# Revit family: QF_Varimixer_Teddy5L
name_source: partatom
category: Specialty Equipment
units: mm (PartAtom-declared; Revit-internal decimal feet)

## family parameters
Always vertical = Yes
Cut with Voids When Loaded = No
OmniClass Number = 23.40.40.14.14.11
OmniClass Title = Food Mixers
Part Type = Normal
Room Calculation Point = No
Round Connector Dimension = Use Diameter
Shared = No
Work Plane-Based = No

## types (15) — shared parameters
Bowl size = 5 liter
Connected with neutral = No
Depth = 462 mm  [stored 1.51575 ft]
Depth Clearance = 540 mm
Description = Planetary mixer TEDDY
Electrical connection height = 40 mm  [stored 0.131234 ft]
Height = 400 mm
Homepage = https://www.varimixer.com
Horsepower = 0.4
Ingress protection = IP42
Length = 241 mm
Manufacturer = Varimixer A/S
Model = TEDDY
Number of phases = 1
Plug included = Yes
Power = 300 W
Product description = Planetary mixer, heavy duty for whipping, kneading and mixing
Product name = TEDDY
URL = www.varimixer.com
URL datasheet = https://varimixer.com
Weight in Kilograms = 18
Weight in Pounds = 40

## per-type parameters (varying)
| type | Attachment drive | Color | Cycle | Full load current | Voltage |
| 230V/50-60Hz/1Ph/Red | No | QF_Plastic-Red-Smooth | 50 Hz | 2 A | 230 V |
| 230V/50-60Hz/1Ph/White | No | QF_Plastic-White-Smooth | 50 Hz | 2 A | 230 V |
| 230V/50-60Hz/1Ph/Silver | No | QF_Metal-Stainless-Satin Brushed Heavy | 50 Hz | 2 A | 230 V |
| 230V/50-60Hz/1Ph/Black | No | QF_Plastic-Black-Smooth | 50 Hz | 2 A | 230 V |
| 230V/50-60Hz/1Ph/White atttachmentdrive | Yes | QF_Plastic-White-Smooth | 50 Hz | 2 A | 230 V |
| 115V/50-60Hz/1Ph/Black | No | QF_Plastic-Black-Smooth | 60 Hz | 5 A | 115 V |
| 115V/50-60Hz/1Ph/Red | No | QF_Plastic-Red-Smooth | 60 Hz | 5 A | 115 V |
| 115V/50-60Hz/1Ph/Silver | No | QF_Metal-Stainless-Satin Brushed Heavy | 60 Hz | 5 A | 115 V |
| 115V/50-60Hz/1Ph/White | No | QF_Plastic-White-Smooth | 60 Hz | 5 A | 115 V |
| 115V/50-60Hz/1Ph/White Attachmentdrive | Yes | QF_Plastic-White-Smooth | 60 Hz | 5 A | 115 V |
| 100V/50-60Hz/1Ph/Black | No | QF_Plastic-Black-Smooth | 60 Hz | 5 A | 100 V |
| 100V/50-60Hz/1Ph/Red | No | QF_Plastic-Red-Smooth | 60 Hz | 5 A | 100 V |
| 100V/50-60Hz/1Ph/Silver | No | QF_Metal-Stainless-Satin Brushed Heavy | 60 Hz | 5 A | 100 V |
| 100V/50-60Hz/1Ph/White | No | QF_Plastic-White-Smooth | 60 Hz | 5 A | 100 V |
| 100V/50-60Hz/1Ph/White Attachmentdrive | Yes | QF_Plastic-White-Smooth | 60 Hz | 5 A | 100 V |

note: [stored X ft] marks values corroborated as IEEE doubles in the binary element streams (Revit-internal decimal feet)

## geometry (parser evidence)
native form markers: Blend x10, Sweep x2
no freeform markers — native parametric forms only
